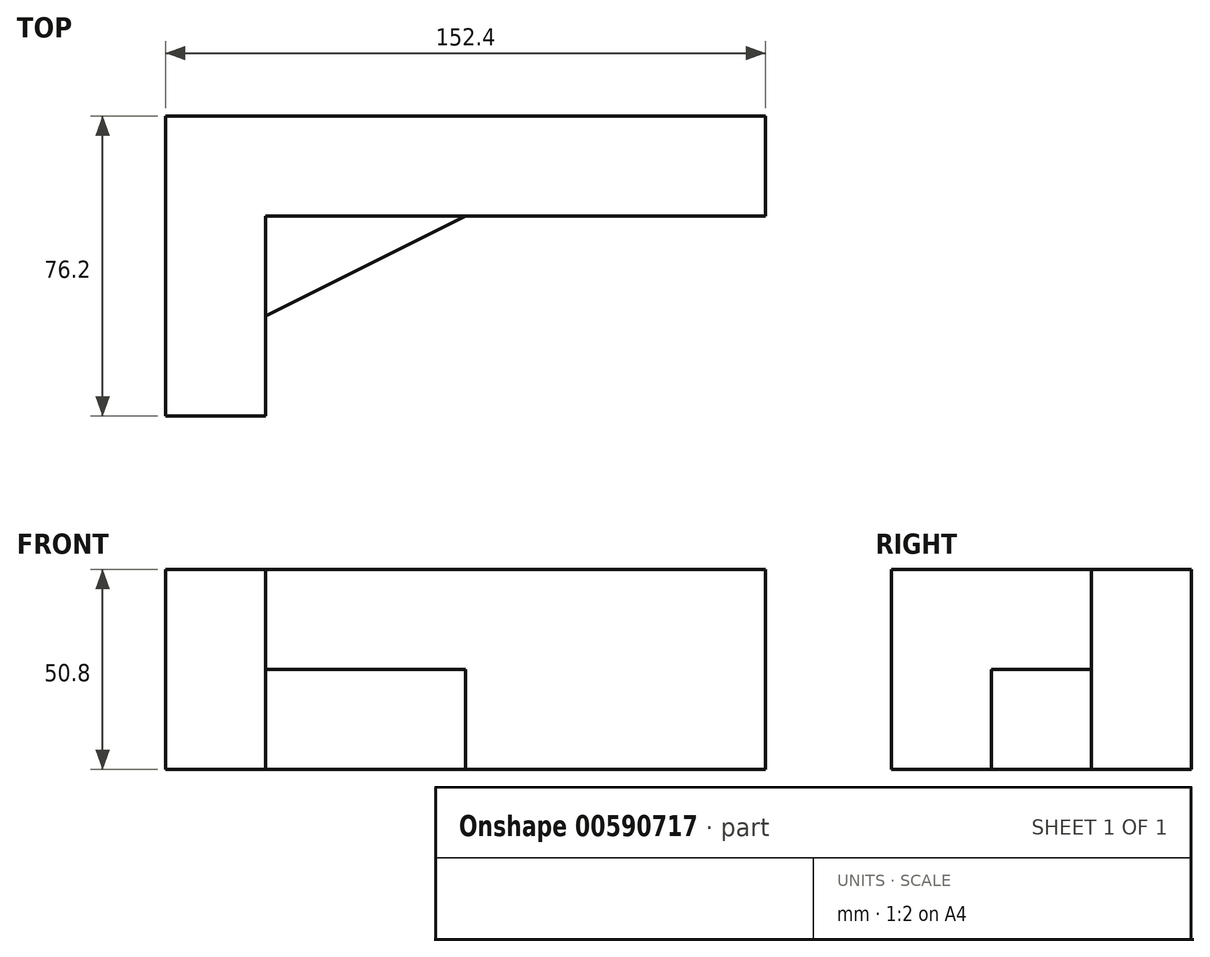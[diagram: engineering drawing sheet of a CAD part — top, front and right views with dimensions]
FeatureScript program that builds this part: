
annotation { "Feature Type Name" : "Feature", "Feature Type Description" : "" }
export const myFeature = defineFeature(function(context is Context, id is Id, definition is map)
    precondition{}
    {
        {
            var Q0;
            Q0=qCreatedBy(makeId("Front.planeOp"),FACE);
            var sketch = newSketch(context, id + "F0", { "sketchPlane" : qUnion([Q0])});
            skLineSegment(sketch, "E0.bottom", {"start": v(0, 0) * mm, "end": v(25.4, 0) * mm});
            skLineSegment(sketch, "E0.top", {"start": v(0, 50.8) * mm, "end": v(25.4, 50.8) * mm});
            skLineSegment(sketch, "E0.left", {"start": v(0, 0) * mm, "end": v(0, 50.8) * mm});
            skLineSegment(sketch, "E0.right", {"start": v(25.4, 0) * mm, "end": v(25.4, 50.8) * mm});
            skSolve(sketch);
        }
        {
            var Q0;
            Q0=makeQuery(id+"F0.imprint","IMPRINT",FACE,{"disambiguationData":[TD([[makeQuery(id+"F0.imprint","IMPRINT",EDGE,{"derivedFrom":sQuery(id+"F0.wireOp",EDGE,"E0.bottom")}),1.0]])]});
            extrude(context, id + "F1", {"entities" : qUnion([Q0]), "depth" : 76.2 * mm, "offsetDistance" : 25.4 * mm});
        }
        {
            var Q0;
            Q0=makeQuery(id+"F1.opExtrude","CAP_FACE",FACE,{"disambiguationData":[OSD([sQuery(id+"F0.wireOp",EDGE,"E0.bottom"),sQuery(id+"F0.wireOp",EDGE,"E0.top"),sQuery(id+"F0.wireOp",EDGE,"E0.left"),sQuery(id+"F0.wireOp",EDGE,"E0.right")])],"isStart":true});
            var sketch = newSketch(context, id + "F2", { "sketchPlane" : qUnion([Q0])});
            skLineSegment(sketch, "E1.bottom", {"start": v(0, 50.8) * mm, "end": v(-152.4, 50.8) * mm});
            skLineSegment(sketch, "E1.top", {"start": v(0, 0) * mm, "end": v(-152.4, 0) * mm});
            skLineSegment(sketch, "E1.left", {"start": v(0, 50.8) * mm, "end": v(0, 0) * mm});
            skLineSegment(sketch, "E1.right", {"start": v(-152.4, 50.8) * mm, "end": v(-152.4, 0) * mm});
            skSolve(sketch);
        }
        {
            var Q0;
            {var subQ2=sQuery(id+"F2.wireOp",EDGE,"E1.right");Q0=makeQuery(id+"F2.imprint","IMPRINT",FACE,{"disambiguationData":[TD([[makeQuery(id+"F2.imprint","IMPRINT",EDGE,{"derivedFrom":subQ2}),1.0]])]});}
            var Q1;
            {var subQ0=sQuery(id+"F2.wireOp",EDGE,"E1.left");Q1=makeQuery(id+"F2.imprint","IMPRINT",FACE,{"disambiguationData":[TD([[makeQuery(id+"F2.imprint","IMPRINT",EDGE,{"derivedFrom":subQ0}),1.0]])]});}
            extrude(context, id + "F3", {"entities" : qUnion([Q0, Q1]), "operationType" : NewBodyOperationType.ADD, "oppositeDirection" : true, "depth" : 25.4 * mm, "offsetDistance" : 25.4 * mm});
        }
        {
            var Q0;
            Q0=qCreatedBy(makeId("Top.planeOp"),FACE);
            var sketch = newSketch(context, id + "F4", { "sketchPlane" : qUnion([Q0])});
            skLineSegment(sketch, "E2", {"start": v(25.4, -25.4) * mm, "end": v(76.2, -25.4) * mm});
            skLineSegment(sketch, "E3", {"start": v(25.4, -25.4) * mm, "end": v(25.4, -50.8) * mm});
            skLineSegment(sketch, "E4", {"start": v(76.2, -25.4) * mm, "end": v(25.4, -50.8) * mm});
            skSolve(sketch);
        }
        {
            var Q0;
            Q0=makeQuery(id+"F4.imprint","IMPRINT",FACE,{"disambiguationData":[TD([[makeQuery(id+"F4.imprint","IMPRINT",EDGE,{"derivedFrom":sQuery(id+"F4.wireOp",EDGE,"E2")}),-1.0]])]});
            extrude(context, id + "F5", {"entities" : qUnion([Q0]), "operationType" : NewBodyOperationType.ADD, "depth" : 25.4 * mm, "offsetDistance" : 25.4 * mm});
        }
    });
